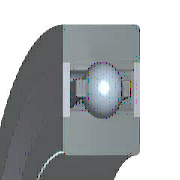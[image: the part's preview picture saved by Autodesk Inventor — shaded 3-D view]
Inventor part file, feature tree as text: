
AUTODESK INVENTOR PART (.ipt)
format: ipt  version: 2019 (Build 230136000, 136)  size: 405,504 bytes
history: native  units: mm
features: sketch x2
ambient origin geometry x8: Origin, YZ Plane, XZ Plane, XY Plane, X Axis, Y Axis, Z Axis, Center Point
bodies: Solid1 (feature_tree)
feature tree (2):
  sketch  "Sketch1"  dims[d1=55.0mm]
  sketch  "Sketch2"  dims[d2=17.9mm d3=30.0mm d5=4.363323mm d8=6.5mm d10=46.85mm d28=14.4mm d29=15.2mm d30=12.0mm d31=39.89mm d32=1.0mm d33=0.6mm d34=1.0mm d35=1.0mm d36=16.0mm d37=38.15mm d40=4.363323mm d41=6.5mm d42=90.0deg d43=90.0deg d44=100.0mm d45=360.0deg d47=0.0mm d48=0.0mm d49=0.0mm d50=0.0mm d51=0.0mm]
